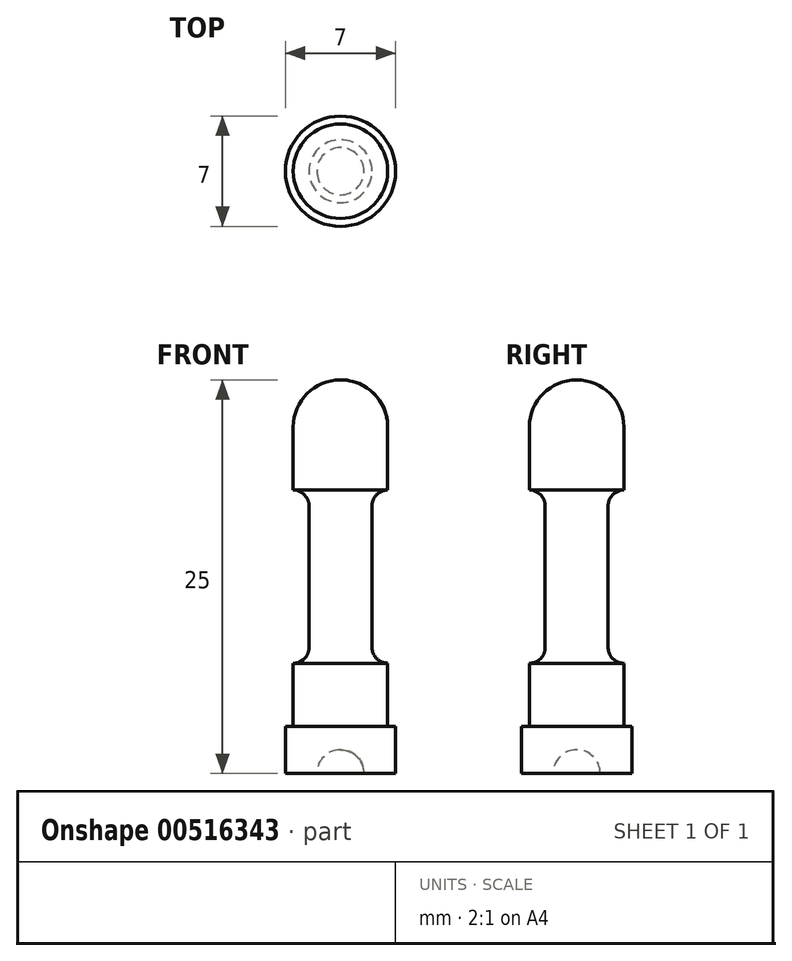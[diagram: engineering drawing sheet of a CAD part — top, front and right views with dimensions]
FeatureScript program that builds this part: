
annotation { "Feature Type Name" : "Feature", "Feature Type Description" : "" }
export const myFeature = defineFeature(function(context is Context, id is Id, definition is map)
    precondition{}
    {
        {
            var Q0;
            Q0=qCreatedBy(makeId("Front.planeOp"),FACE);
            var sketch = newSketch(context, id + "F0", { "sketchPlane" : qUnion([Q0])});
            skLineSegment(sketch, "E0", {"start": v(0, 0) * mm, "end": v(3.5, 0) * mm});
            skLineSegment(sketch, "E1", {"start": v(3.5, 0) * mm, "end": v(3.5, 3) * mm});
            skLineSegment(sketch, "E2", {"start": v(3.5, 3) * mm, "end": v(3, 3) * mm});
            skLineSegment(sketch, "E3", {"start": v(3, 3) * mm, "end": v(3, 7) * mm});
            skLineSegment(sketch, "E4", {"start": v(3, 7) * mm, "end": v(3, 7) * mm});
            skLineSegment(sketch, "E5", {"start": v(2, 8) * mm, "end": v(2, 17) * mm});
            skLineSegment(sketch, "E6", {"start": v(3, 18) * mm, "end": v(3, 18) * mm});
            skLineSegment(sketch, "E7", {"start": v(3, 18) * mm, "end": v(3, 22) * mm});
            skArc(sketch, "E8", {"start": v(3, 22) * mm, "mid": v(2.12, 24.12) * mm, "end": v(0, 25) * mm});
            skLineSegment(sketch, "E9", {"start": v(0, 25) * mm, "end": v(0, 0) * mm});
            skPoint(sketch, "E10.visualSharp", {"position": v(2, 7) * mm});
            skArc(sketch, "E10.filletArc", {"start": v(2, 8) * mm, "mid": v(2.3, 7.3) * mm, "end": v(3, 7) * mm});
            skPoint(sketch, "E11.visualSharp", {"position": v(2, 18) * mm});
            skArc(sketch, "E11.filletArc", {"start": v(3, 18) * mm, "mid": v(2.3, 17.7) * mm, "end": v(2, 17) * mm});
            skSolve(sketch);
        }
        {
            var Q0;
            Q0=makeQuery(id+"F0.imprint","IMPRINT",FACE,{"disambiguationData":[TD([[makeQuery(id+"F0.imprint","IMPRINT",EDGE,{"derivedFrom":sQuery(id+"F0.wireOp",EDGE,"E0")}),1.0]])]});
            var Q1;
            Q1=sQuery(id+"F0.wireOp",EDGE,"E0");
            var Q2;
            Q2=sQuery(id+"F0.wireOp",EDGE,"E8");
            var Q3;
            Q3=sQuery(id+"F0.wireOp",EDGE,"E7");
            var Q4;
            Q4=sQuery(id+"F0.wireOp",EDGE,"E5");
            var Q5;
            Q5=sQuery(id+"F0.wireOp",EDGE,"E3");
            var Q6;
            Q6=sQuery(id+"F0.wireOp",EDGE,"E1");
            var Q7;
            Q7=sQuery(id+"F0.wireOp",EDGE,"E11.filletArc");
            var Q8;
            Q8=sQuery(id+"F0.wireOp",EDGE,"E10.filletArc");
            var Q9;
            Q9=sQuery(id+"F0.wireOp",EDGE,"E2");
            var Q10;
            Q10=sQuery(id+"F0.wireOp",EDGE,"E9");
            revolve(context, id + "F1", {"entities" : qUnion([Q0]), "surfaceEntities" : qUnion([Q1, Q2, Q3, Q4, Q5, Q6, Q7, Q8, Q9]), "axis" : qUnion([Q10]), "revolveType" : RevolveType.FULL});
        }
        {
            var Q0;
            Q0=qCreatedBy(makeId("Front.planeOp"),FACE);
            var sketch = newSketch(context, id + "F2", { "sketchPlane" : qUnion([Q0])});
            skLineSegment(sketch, "E12", {"start": v(0, 0) * mm, "end": v(1.5, 0) * mm});
            skLineSegment(sketch, "E13", {"start": v(0, 1.5) * mm, "end": v(0, 0) * mm});
            skArc(sketch, "E14", {"start": v(1.5, 0) * mm, "mid": v(1.06, 1.06) * mm, "end": v(0, 1.5) * mm});
            skSolve(sketch);
        }
        {
            var Q0;
            Q0 = qSketchRegion(id + "F2", true);
            var Q1;
            Q1=sQuery(id+"F2.wireOp",EDGE,"E13");
            revolve(context, id + "F3", {"operationType" : NewBodyOperationType.REMOVE, "entities" : qUnion([Q0]), "axis" : qUnion([Q1]), "revolveType" : RevolveType.FULL, "oppositeDirection" : true});
        }
    });
